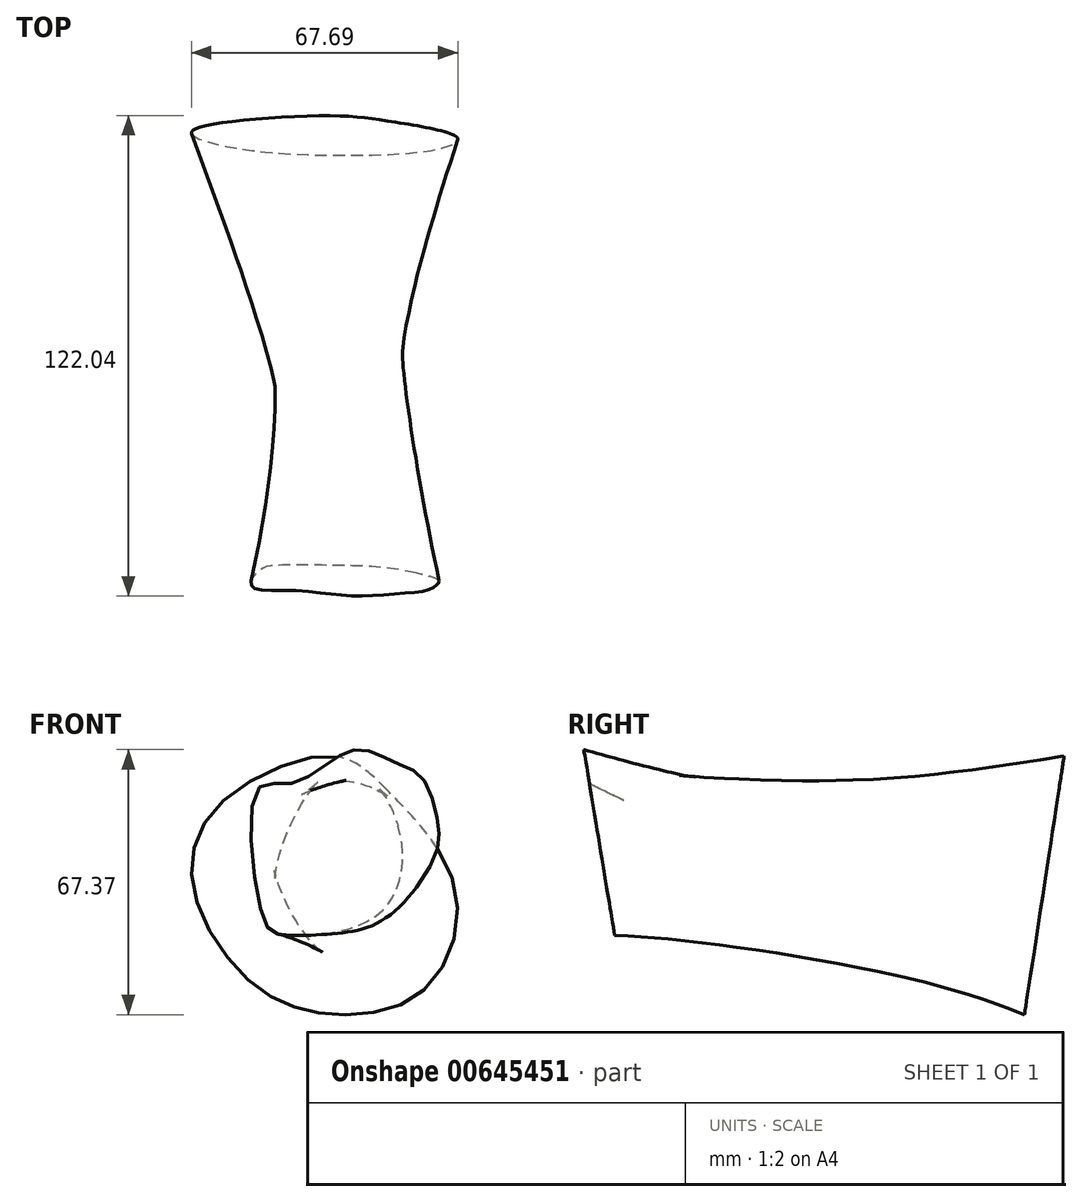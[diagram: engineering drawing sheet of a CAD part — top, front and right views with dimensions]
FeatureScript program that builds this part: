
annotation { "Feature Type Name" : "Feature", "Feature Type Description" : "" }
export const myFeature = defineFeature(function(context is Context, id is Id, definition is map)
    precondition{}
    {
        {
            var Q0;
            Q0=qCreatedBy(makeId("Right.planeOp"),FACE);
            var sketch = newSketch(context, id + "F0", { "sketchPlane" : qUnion([Q0])});
            skFitSpline(sketch, "E0", {"points": [v(-56.45, 36.34) * mm, v(-41.65, 46.59) * mm, v(-14.33, 53.8) * mm, v(-9.77, 54.37) * mm, v(25.52, 53.42) * mm, v(58.54, 29.32) * mm, v(83.02, -4.08) * mm, v(78.09, -19.83) * mm, v(61.96, -25.9) * mm, v(42.22, -36.72) * mm, v(17.36, -45.07) * mm, v(2.56, -46.4) * mm, v(-19.26, -37.67) * mm, v(-39, -26.66) * mm, v(-53.6, -15.47) * mm, v(-61.2, -12.24) * mm, v(-71.06, -1.61) * mm, v(-75.05, 5.6) * mm, v(-76.76, 15.28) * mm, v(-73.53, 22.68) * mm, v(-56.45, 36.34) * mm]});
            skLineSegment(sketch, "E1", {"start": v(-71.63, 71.06) * mm, "end": v(-50.95, -53.23) * mm});
            skLineSegment(sketch, "E2", {"start": v(63.1, 72.58) * mm, "end": v(43.55, -54.94) * mm});
            skSolve(sketch);
        }
        {
            var Q0;
            Q0=sQuery(id+"F0.wireOp",EDGE,"E1");
            cPlane(context, id + "F1", {"entities" : qUnion([Q0]), "cplaneType" : CPlaneType.LINE_ANGLE, "offset" : 25 * mm, "angle" : 90 * degree, "width" : 150 * mm, "height" : 150 * mm});
        }
        {
            var Q0;
            Q0=sQuery(id+"F0.wireOp",EDGE,"E2");
            cPlane(context, id + "F2", {"entities" : qUnion([Q0]), "cplaneType" : CPlaneType.LINE_ANGLE, "offset" : 25 * mm, "angle" : 90 * degree, "width" : 150 * mm, "height" : 150 * mm});
        }
        {
            var Q0;
            Q0=qCreatedBy(id+"F1.planeOp",FACE);
            var sketch = newSketch(context, id + "F3", { "sketchPlane" : qUnion([Q0])});
            skFitSpline(sketch, "E3", {"points": [v(18.7, 33.04) * mm, v(10.63, 34.4) * mm, v(0, 40.26) * mm, v(-7.67, 43.15) * mm, v(-16.21, 39.79) * mm, v(-23.01, 36.06) * mm, v(-26.98, 24.42) * mm, v(-26.45, 16.12) * mm, v(-14.14, 0) * mm, v(0, -4.3) * mm, v(13.36, -4.4) * mm, v(17.43, 0) * mm, v(18.7, 33.04) * mm]});
            skSolve(sketch);
        }
        {
            var Q0;
            Q0=qCreatedBy(id+"F2.planeOp",FACE);
            var sketch = newSketch(context, id + "F4", { "sketchPlane" : qUnion([Q0])});
            skFitSpline(sketch, "E4", {"points": [v(-14.2, 30.67) * mm, v(0, 39.43) * mm, v(28.18, 27.3) * mm, v(35.14, 5.75) * mm, v(19.57, -19.42) * mm, v(0, -26.84) * mm, v(-22.93, -21.13) * mm, v(-31.53, 5.03) * mm, v(-14.2, 30.67) * mm]});
            skSolve(sketch);
        }
        {
            var Q0;
            Q0=makeQuery(id+"F4.imprint","IMPRINT",FACE,{"disambiguationData":[TD([[makeQuery(id+"F4.imprint","IMPRINT",EDGE,{"derivedFrom":sQuery(id+"F4.wireOp",EDGE,"E4")}),-1.0]])]});
            var Q1;
            Q1=makeQuery(id+"F3.imprint","IMPRINT",FACE,{"disambiguationData":[TD([[makeQuery(id+"F3.imprint","IMPRINT",EDGE,{"derivedFrom":sQuery(id+"F3.wireOp",EDGE,"E3")}),1.0]])]});
            loft(context, id + "F5", {"sheetProfilesArray" : [{ "sheetProfileEntities" : qUnion([Q0]) }, { "sheetProfileEntities" : qUnion([Q1]) }]});
        }
    });
